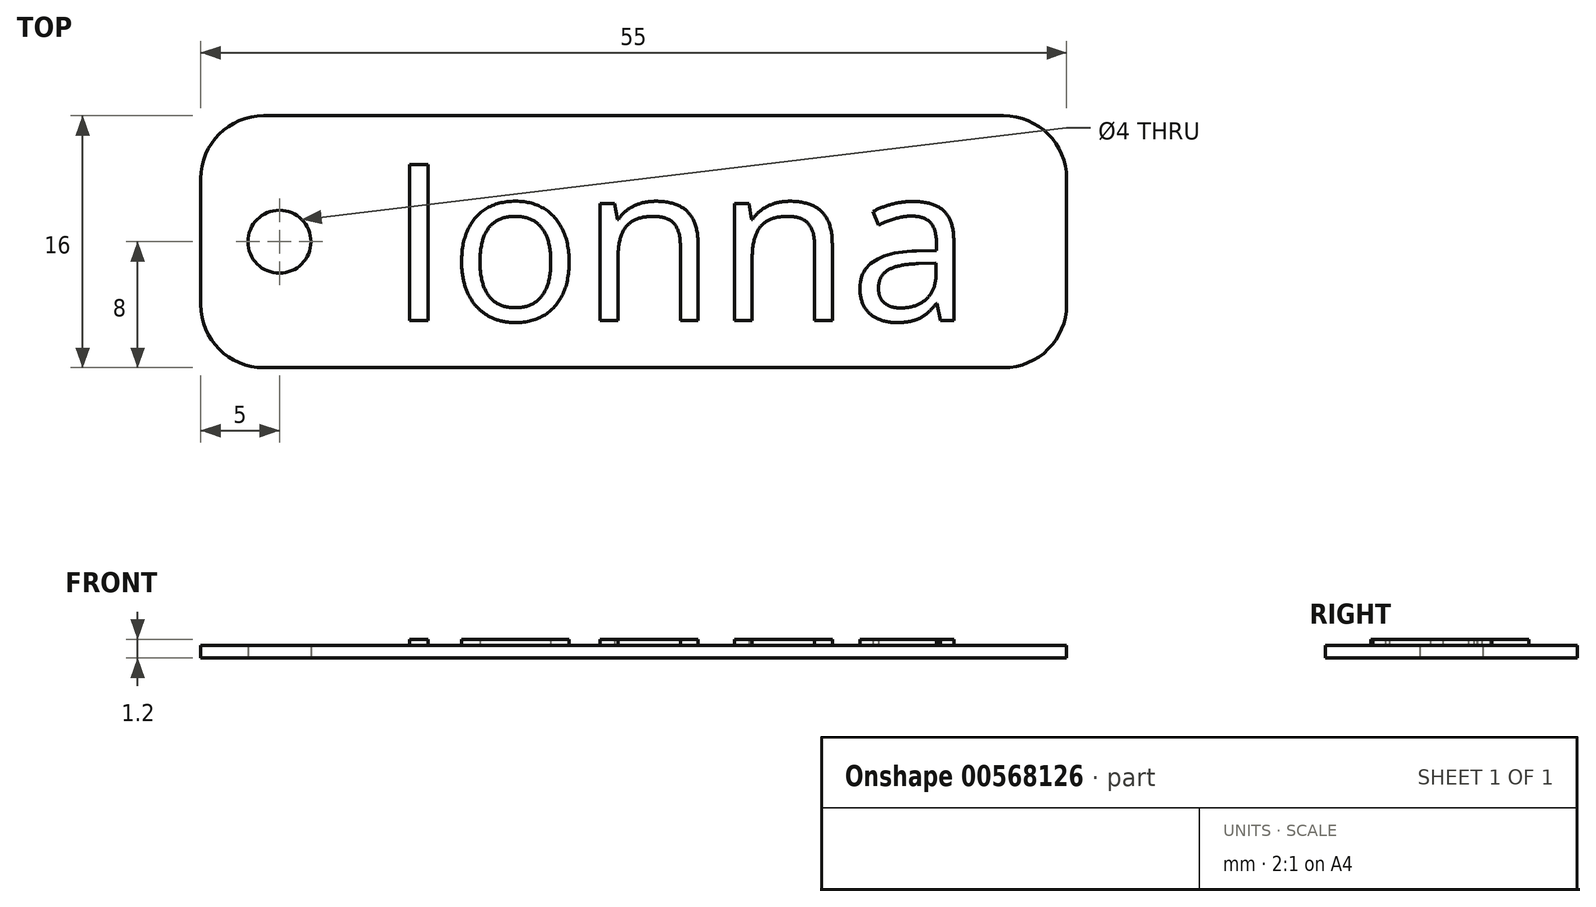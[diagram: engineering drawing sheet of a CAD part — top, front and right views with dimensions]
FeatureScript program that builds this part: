
annotation { "Feature Type Name" : "Feature", "Feature Type Description" : "" }
export const myFeature = defineFeature(function(context is Context, id is Id, definition is map)
    precondition{}
    {
        {
            var Q0;
            Q0=qCreatedBy(makeId("Top.planeOp"),FACE);
            var sketch = newSketch(context, id + "F0", { "sketchPlane" : qUnion([Q0])});
            skLineSegment(sketch, "E0.bottom", {"start": v(-27.5, 8) * mm, "end": v(27.5, 8) * mm});
            skLineSegment(sketch, "E0.top", {"start": v(-27.5, -8) * mm, "end": v(27.5, -8) * mm});
            skLineSegment(sketch, "E0.left", {"start": v(-27.5, 8) * mm, "end": v(-27.5, -8) * mm});
            skLineSegment(sketch, "E0.right", {"start": v(27.5, 8) * mm, "end": v(27.5, -8) * mm});
            skCircle(sketch, "E1", {"center": v(-22.5, 0) * mm, "radius": 2 * mm});
            skSolve(sketch);
        }
        {
            var Q0;
            Q0=makeQuery(id+"F0.imprint","IMPRINT",FACE,{"disambiguationData":[TD([[makeQuery(id+"F0.imprint","IMPRINT",EDGE,{"derivedFrom":sQuery(id+"F0.wireOp",EDGE,"E0.bottom")}),-1.0]])]});
            extrude(context, id + "F1", {"entities" : qUnion([Q0]), "depth" : 0.8 * mm, "offsetDistance" : 25 * mm});
        }
        {
            var Q0;
            Q0=makeQuery(id+"F1.opExtrude","CAP_FACE",FACE,{"disambiguationData":[OSD([sQuery(id+"F0.wireOp",EDGE,"E0.bottom"),sQuery(id+"F0.wireOp",EDGE,"E0.top"),sQuery(id+"F0.wireOp",EDGE,"E0.left"),sQuery(id+"F0.wireOp",EDGE,"E0.right")])],"isStart":false});
            var sketch = newSketch(context, id + "F2", { "sketchPlane" : qUnion([Q0])});
            skText(sketch, "E2", { "text": "Ionna", "fontName": "OpenSans-Regular.ttf"});
            const initialGuessF2  = {"E2": [-0.01558, -0.005, 1, 0, 0.01]};
            skSetInitialGuess(sketch, initialGuessF2);
            skSolve(sketch);
        }
        {
            var Q0;
            Q0 = qSketchRegion(id + "F2", true);
            extrude(context, id + "F3", {"entities" : qUnion([Q0]), "operationType" : NewBodyOperationType.ADD, "depth" : 0.4 * mm, "offsetDistance" : 25 * mm});
        }
        {
            var Q0;
            Q0=makeQuery(id+"F1.opExtrude","SWEPT_EDGE",EDGE,{"disambiguationData":[OSD([sQuery(id+"F0.wireOp",EDGE,"E0.top"),sQuery(id+"F0.wireOp",EDGE,"E0.left")])]});
            var Q1;
            Q1=makeQuery(id+"F1.opExtrude","SWEPT_EDGE",EDGE,{"disambiguationData":[OSD([sQuery(id+"F0.wireOp",EDGE,"E0.top"),sQuery(id+"F0.wireOp",EDGE,"E0.right")])]});
            var Q2;
            Q2=makeQuery(id+"F1.opExtrude","SWEPT_EDGE",EDGE,{"disambiguationData":[OSD([sQuery(id+"F0.wireOp",EDGE,"E0.bottom"),sQuery(id+"F0.wireOp",EDGE,"E0.right")])]});
            var Q3;
            Q3=makeQuery(id+"F1.opExtrude","SWEPT_EDGE",EDGE,{"disambiguationData":[OSD([sQuery(id+"F0.wireOp",EDGE,"E0.bottom"),sQuery(id+"F0.wireOp",EDGE,"E0.left")])]});
            fillet(context, id + "F4", {"entities" : qUnion([Q0, Q1, Q2, Q3]), "radius" : 4 * mm, "tangentPropagation" : true, "allowEdgeOverflow" : false});
        }
    });
